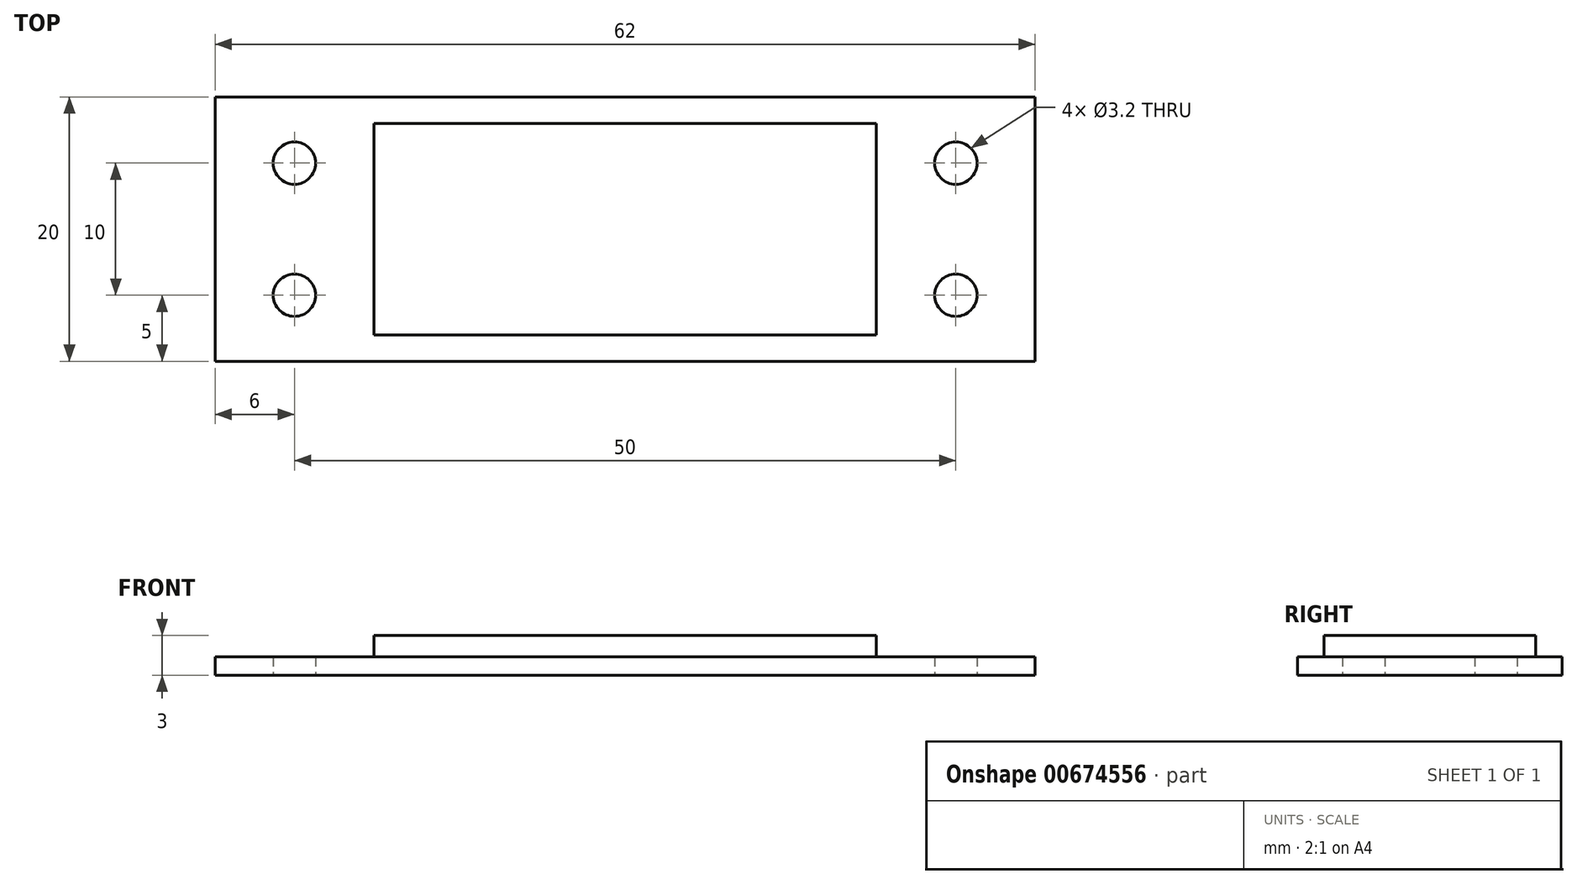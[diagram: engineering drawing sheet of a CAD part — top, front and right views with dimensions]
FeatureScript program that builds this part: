
annotation { "Feature Type Name" : "Feature", "Feature Type Description" : "" }
export const myFeature = defineFeature(function(context is Context, id is Id, definition is map)
    precondition{}
    {
        {
            var Q0;
            Q0=qCreatedBy(makeId("Top.planeOp"),FACE);
            var sketch = newSketch(context, id + "F0", { "sketchPlane" : qUnion([Q0])});
            skLineSegment(sketch, "E0.bottom", {"start": v(0, 0) * mm, "end": v(62, 0) * mm});
            skLineSegment(sketch, "E0.top", {"start": v(0, 20) * mm, "end": v(62, 20) * mm});
            skLineSegment(sketch, "E0.left", {"start": v(0, 0) * mm, "end": v(0, 20) * mm});
            skLineSegment(sketch, "E0.right", {"start": v(62, 0) * mm, "end": v(62, 20) * mm});
            skCircle(sketch, "E1", {"center": v(6, 15) * mm, "radius": 1.6 * mm});
            skCircle(sketch, "E2", {"center": v(6, 5) * mm, "radius": 1.6 * mm});
            skCircle(sketch, "E3", {"center": v(56, 15) * mm, "radius": 1.6 * mm});
            skCircle(sketch, "E4", {"center": v(56, 5) * mm, "radius": 1.6 * mm});
            skSolve(sketch);
        }
        {
            var Q0;
            Q0 = qSketchRegion(id + "F0", true);
            extrude(context, id + "F1", {"entities" : qUnion([Q0]), "depth" : 1.4 * mm, "offsetDistance" : 25 * mm});
        }
        {
            var Q0;
            Q0=makeQuery(id+"F1.opExtrude","CAP_FACE",FACE,{"disambiguationData":[OSD([sQuery(id+"F0.wireOp",EDGE,"E0.bottom"),sQuery(id+"F0.wireOp",EDGE,"E0.top"),sQuery(id+"F0.wireOp",EDGE,"E0.left"),sQuery(id+"F0.wireOp",EDGE,"E0.right"),sQuery(id+"F0.wireOp",EDGE,"E1"),sQuery(id+"F0.wireOp",EDGE,"E2"),sQuery(id+"F0.wireOp",EDGE,"E3"),sQuery(id+"F0.wireOp",EDGE,"E4")])],"isStart":false});
            var sketch = newSketch(context, id + "F2", { "sketchPlane" : qUnion([Q0])});
            skLineSegment(sketch, "E5.bottom", {"start": v(12, 18) * mm, "end": v(50, 18) * mm});
            skLineSegment(sketch, "E5.top", {"start": v(12, 2) * mm, "end": v(50, 2) * mm});
            skLineSegment(sketch, "E5.left", {"start": v(12, 18) * mm, "end": v(12, 2) * mm});
            skLineSegment(sketch, "E5.right", {"start": v(50, 18) * mm, "end": v(50, 2) * mm});
            skSolve(sketch);
        }
        {
            var Q0;
            Q0 = qSketchRegion(id + "F2", true);
            extrude(context, id + "F3", {"entities" : qUnion([Q0]), "operationType" : NewBodyOperationType.ADD, "depth" : 1.6 * mm, "offsetDistance" : 25 * mm});
        }
    });
